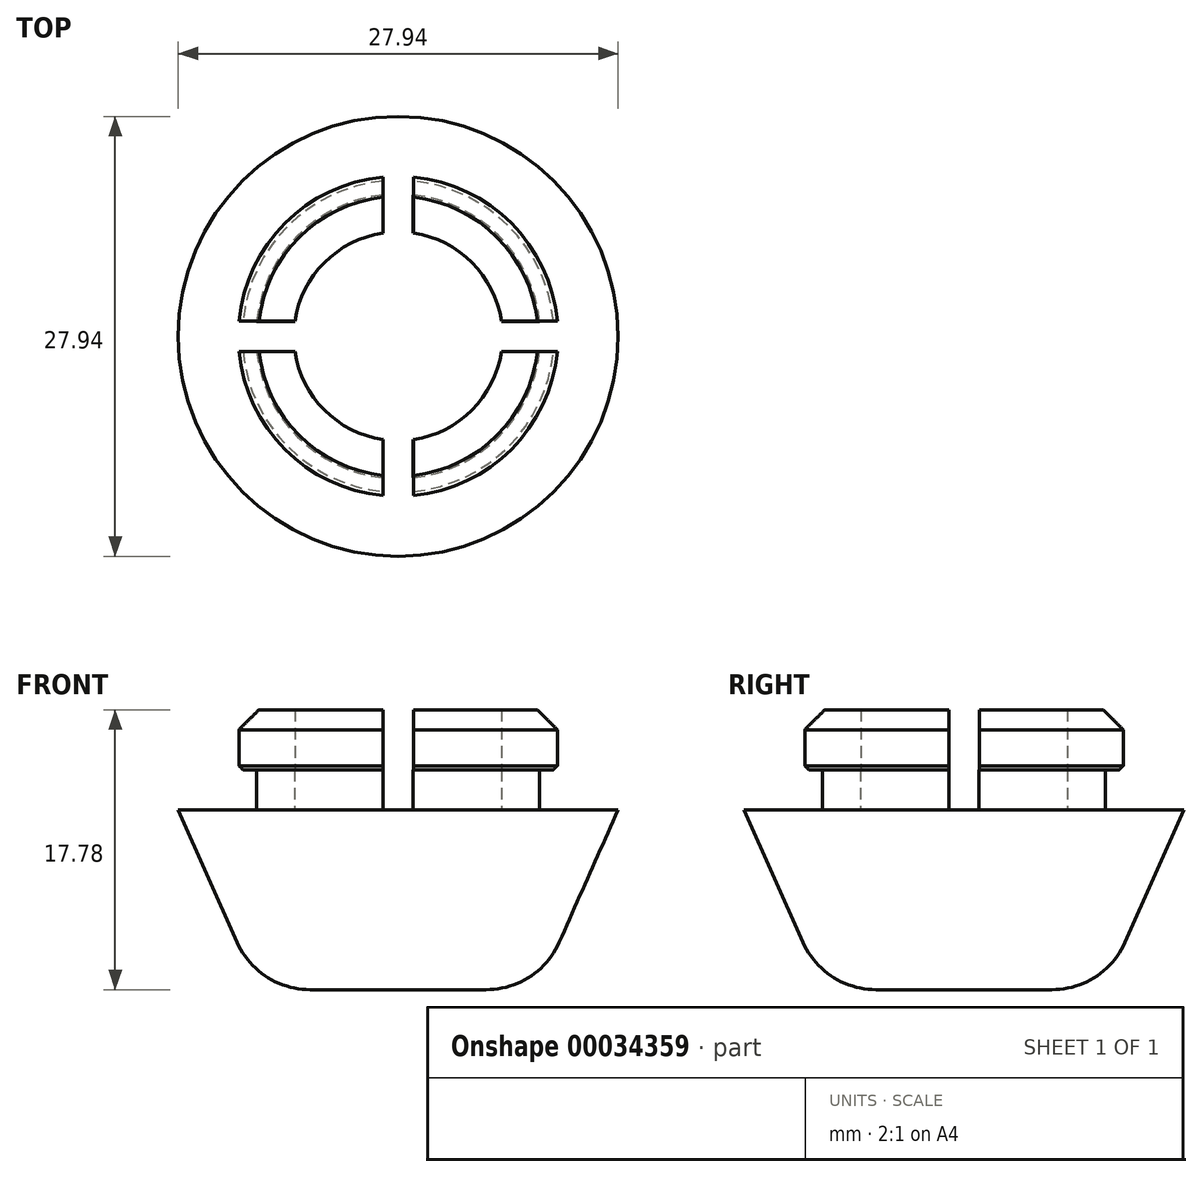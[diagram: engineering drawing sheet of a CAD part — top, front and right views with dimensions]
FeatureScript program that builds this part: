
annotation { "Feature Type Name" : "Feature", "Feature Type Description" : "" }
export const myFeature = defineFeature(function(context is Context, id is Id, definition is map)
    precondition{}
    {
        {
            var Q0;
            Q0=qCreatedBy(makeId("Top.planeOp"),FACE);
            cPlane(context, id + "F0", {"entities" : qUnion([Q0]), "cplaneType" : CPlaneType.OFFSET, "offset" : 11.43 * mm, "width" : 152.4 * mm, "height" : 152.4 * mm});
        }
        {
            var Q0;
            Q0=qCreatedBy(makeId("Top.planeOp"),FACE);
            var sketch = newSketch(context, id + "F1", { "sketchPlane" : qUnion([Q0])});
            skCircle(sketch, "E0", {"center": v(0, 0) * mm, "radius": 8.9 * mm});
            skSolve(sketch);
        }
        {
            var Q0;
            Q0=qCreatedBy(id+"F0.planeOp",FACE);
            var sketch = newSketch(context, id + "F2", { "sketchPlane" : qUnion([Q0])});
            skCircle(sketch, "E1", {"center": v(0, 0) * mm, "radius": 13.97 * mm});
            skSolve(sketch);
        }
        {
            var Q0;
            Q0=qCreatedBy(id+"F0.planeOp",FACE);
            cPlane(context, id + "F3", {"entities" : qUnion([Q0]), "cplaneType" : CPlaneType.OFFSET, "offset" : 2.54 * mm, "width" : 152.4 * mm, "height" : 152.4 * mm});
        }
        {
            var Q0;
            Q0 = qSketchRegion(id + "F1", true);
            var Q1;
            Q1 = qSketchRegion(id + "F2", true);
            loft(context, id + "F4", {"sheetProfilesArray" : [{ "sheetProfileEntities" : qUnion([Q0]) }, { "sheetProfileEntities" : qUnion([Q1]) }]});
        }
        {
            var Q0;
            Q0=makeQuery(id+"F4.opLoft","MID_CAP_EDGE",EDGE,{"disambiguationData":[OSD([sQuery(id+"F1.wireOp",EDGE,"E0")])],"capPos":0.0});
            fillet(context, id + "F5", {"entities" : qUnion([Q0]), "radius" : 5.08 * mm, "tangentPropagation" : true, "allowEdgeOverflow" : false});
        }
        {
            var Q0;
            Q0=qCreatedBy(id+"F0.planeOp",FACE);
            var sketch = newSketch(context, id + "F6", { "sketchPlane" : qUnion([Q0])});
            skArc(sketch, "E2", {"start": v(-0.95, 8.98) * mm, "mid": v(-6.39, 6.39) * mm, "end": v(-8.98, 0.95) * mm});
            skLineSegment(sketch, "E3.rect.bottom", {"start": v(8.98, -0.95) * mm, "end": v(6.57, -0.95) * mm});
            skLineSegment(sketch, "E3.rect.top", {"start": v(8.98, 0.95) * mm, "end": v(6.57, 0.95) * mm});
            skLineSegment(sketch, "E4.rect.left", {"start": v(-0.95, 8.98) * mm, "end": v(-0.95, 6.57) * mm});
            skLineSegment(sketch, "E4.rect.right", {"start": v(0.95, 8.98) * mm, "end": v(0.95, 6.57) * mm});
            skLineSegment(sketch, "E5.trimOffspring", {"start": v(-6.57, -0.95) * mm, "end": v(-8.98, -0.95) * mm});
            skLineSegment(sketch, "E6.trimOffspring", {"start": v(-0.95, -6.57) * mm, "end": v(-0.95, -8.98) * mm});
            skLineSegment(sketch, "E7.trimOffspring", {"start": v(-6.57, 0.95) * mm, "end": v(-8.98, 0.95) * mm});
            skLineSegment(sketch, "E8.trimOffspring", {"start": v(0.95, -6.57) * mm, "end": v(0.95, -8.98) * mm});
            skArc(sketch, "E9.trimOffspring", {"start": v(8.98, 0.95) * mm, "mid": v(6.39, 6.39) * mm, "end": v(0.95, 8.98) * mm});
            skArc(sketch, "E10.trimOffspring", {"start": v(0.95, -8.98) * mm, "mid": v(6.39, -6.39) * mm, "end": v(8.98, -0.95) * mm});
            skArc(sketch, "E11.trimOffspring", {"start": v(-8.98, -0.95) * mm, "mid": v(-6.39, -6.39) * mm, "end": v(-0.95, -8.98) * mm});
            skArc(sketch, "E12", {"start": v(6.57, 0.95) * mm, "mid": v(4.7, 4.7) * mm, "end": v(0.95, 6.57) * mm});
            skArc(sketch, "E13.trimOffspring", {"start": v(-0.95, 6.57) * mm, "mid": v(-4.7, 4.7) * mm, "end": v(-6.57, 0.95) * mm});
            skArc(sketch, "E14.trimOffspring", {"start": v(-6.57, -0.95) * mm, "mid": v(-4.7, -4.7) * mm, "end": v(-0.95, -6.57) * mm});
            skArc(sketch, "E15.trimOffspring", {"start": v(0.95, -6.57) * mm, "mid": v(4.7, -4.7) * mm, "end": v(6.57, -0.95) * mm});
            skSolve(sketch);
        }
        {
            var Q0;
            Q0=makeQuery(id+"F6.imprint","IMPRINT",FACE,{"disambiguationData":[TD([[makeQuery(id+"F6.imprint","IMPRINT",EDGE,{"derivedFrom":sQuery(id+"F6.wireOp",EDGE,"E2")}),1.0]])]});
            var Q1;
            Q1=makeQuery(id+"F6.imprint","IMPRINT",FACE,{"disambiguationData":[TD([[makeQuery(id+"F6.imprint","IMPRINT",EDGE,{"derivedFrom":sQuery(id+"F6.wireOp",EDGE,"E5.trimOffspring")}),1.0]])]});
            var Q2;
            Q2=makeQuery(id+"F6.imprint","IMPRINT",FACE,{"disambiguationData":[TD([[makeQuery(id+"F6.imprint","IMPRINT",EDGE,{"derivedFrom":sQuery(id+"F6.wireOp",EDGE,"E3.rect.bottom")}),1.0]])]});
            var Q3;
            Q3=makeQuery(id+"F6.imprint","IMPRINT",FACE,{"disambiguationData":[TD([[makeQuery(id+"F6.imprint","IMPRINT",EDGE,{"derivedFrom":sQuery(id+"F6.wireOp",EDGE,"E3.rect.top")}),-1.0]])]});
            extrude(context, id + "F7", {"entities" : qUnion([Q0, Q1, Q2, Q3]), "operationType" : NewBodyOperationType.ADD, "depth" : 2.54 * mm});
        }
        {
            var Q0;
            Q0=qCreatedBy(id+"F3.planeOp",FACE);
            var sketch = newSketch(context, id + "F8", { "sketchPlane" : qUnion([Q0])});
            skArc(sketch, "E16", {"start": v(-0.97, 10.11) * mm, "mid": v(-7.18, 7.18) * mm, "end": v(-10.11, 0.97) * mm});
            skArc(sketch, "E17", {"start": v(-0.97, 6.56) * mm, "mid": v(-4.69, 4.69) * mm, "end": v(-6.56, 0.97) * mm});
            skLineSegment(sketch, "E18.rect.left", {"start": v(0.97, 10.11) * mm, "end": v(0.97, 6.56) * mm});
            skLineSegment(sketch, "E18.rect.right", {"start": v(-0.97, 10.11) * mm, "end": v(-0.97, 6.56) * mm});
            skLineSegment(sketch, "E19.rect.bottom", {"start": v(10.11, 0.97) * mm, "end": v(6.56, 0.97) * mm});
            skLineSegment(sketch, "E19.rect.top", {"start": v(10.11, -0.97) * mm, "end": v(6.56, -0.97) * mm});
            skArc(sketch, "E20.trimOffspring", {"start": v(10.11, 0.97) * mm, "mid": v(7.18, 7.18) * mm, "end": v(0.97, 10.11) * mm});
            skArc(sketch, "E21.trimOffspring", {"start": v(6.56, 0.97) * mm, "mid": v(4.69, 4.69) * mm, "end": v(0.97, 6.56) * mm});
            skArc(sketch, "E22.trimOffspring", {"start": v(0.97, -6.56) * mm, "mid": v(4.69, -4.69) * mm, "end": v(6.56, -0.97) * mm});
            skArc(sketch, "E23.trimOffspring", {"start": v(0.97, -10.11) * mm, "mid": v(7.18, -7.18) * mm, "end": v(10.11, -0.97) * mm});
            skArc(sketch, "E24.trimOffspring", {"start": v(-10.11, -0.97) * mm, "mid": v(-7.18, -7.18) * mm, "end": v(-0.97, -10.11) * mm});
            skArc(sketch, "E25.trimOffspring", {"start": v(-6.56, -0.97) * mm, "mid": v(-4.69, -4.69) * mm, "end": v(-0.97, -6.56) * mm});
            skLineSegment(sketch, "E26.trimOffspring", {"start": v(-6.56, 0.97) * mm, "end": v(-10.11, 0.97) * mm});
            skLineSegment(sketch, "E27.trimOffspring", {"start": v(-0.97, -6.56) * mm, "end": v(-0.97, -10.11) * mm});
            skLineSegment(sketch, "E28.trimOffspring", {"start": v(0.97, -6.56) * mm, "end": v(0.97, -10.11) * mm});
            skLineSegment(sketch, "E29.trimOffspring", {"start": v(-6.56, -0.97) * mm, "end": v(-10.11, -0.97) * mm});
            skSolve(sketch);
        }
        {
            var Q0;
            Q0 = qSketchRegion(id + "F8", true);
            extrude(context, id + "F9", {"entities" : qUnion([Q0]), "operationType" : NewBodyOperationType.ADD, "depth" : 3.8 * mm});
        }
        {
            var Q0;
            Q0=makeQuery(id+"F9.opExtrude","CAP_EDGE",EDGE,{"disambiguationData":[OSD([sQuery(id+"F8.wireOp",EDGE,"E24.trimOffspring")])],"isStart":false});
            var Q1;
            Q1=makeQuery(id+"F9.opExtrude","CAP_EDGE",EDGE,{"disambiguationData":[OSD([sQuery(id+"F8.wireOp",EDGE,"E23.trimOffspring")])],"isStart":false});
            var Q2;
            Q2=makeQuery(id+"F9.opExtrude","CAP_EDGE",EDGE,{"disambiguationData":[OSD([sQuery(id+"F8.wireOp",EDGE,"E20.trimOffspring")])],"isStart":false});
            var Q3;
            Q3=makeQuery(id+"F9.opExtrude","CAP_EDGE",EDGE,{"disambiguationData":[OSD([sQuery(id+"F8.wireOp",EDGE,"E16")])],"isStart":false});
            chamfer(context, id + "F10", {"entities" : qUnion([Q0, Q1, Q2, Q3]), "width" : 1.27 * mm, "tangentPropagation" : true});
        }
        {
            var Q0;
            Q0=makeQuery(id+"F9.opExtrude","CAP_EDGE",EDGE,{"disambiguationData":[OSD([sQuery(id+"F8.wireOp",EDGE,"E24.trimOffspring")])],"isStart":true});
            var Q1;
            Q1=makeQuery(id+"F9.opExtrude","CAP_EDGE",EDGE,{"disambiguationData":[OSD([sQuery(id+"F8.wireOp",EDGE,"E16")])],"isStart":true});
            var Q2;
            Q2=makeQuery(id+"F9.opExtrude","CAP_EDGE",EDGE,{"disambiguationData":[OSD([sQuery(id+"F8.wireOp",EDGE,"E23.trimOffspring")])],"isStart":true});
            var Q3;
            Q3=makeQuery(id+"F9.opExtrude","CAP_EDGE",EDGE,{"disambiguationData":[OSD([sQuery(id+"F8.wireOp",EDGE,"E20.trimOffspring")])],"isStart":true});
            chamfer(context, id + "F11", {"entities" : qUnion([Q0, Q1, Q2, Q3]), "width" : 0.25 * mm, "tangentPropagation" : true});
        }
    });
